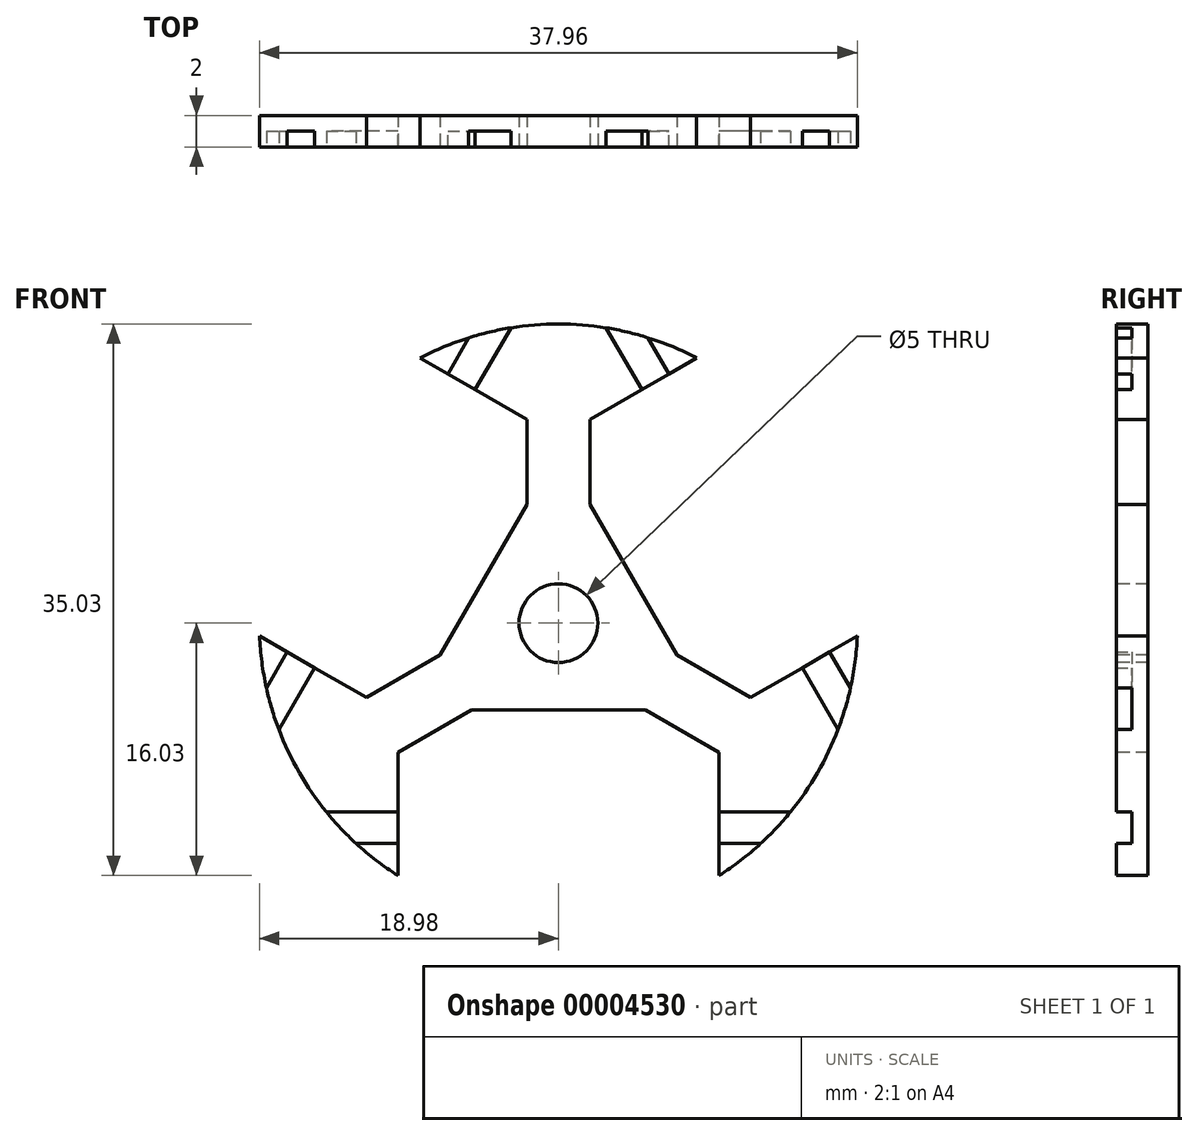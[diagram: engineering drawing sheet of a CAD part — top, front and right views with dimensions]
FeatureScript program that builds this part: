
annotation { "Feature Type Name" : "Feature", "Feature Type Description" : "" }
export const myFeature = defineFeature(function(context is Context, id is Id, definition is map)
    precondition{}
    {
        {
            var Q0;
            Q0=qCreatedBy(makeId("Front.planeOp"),FACE);
            var sketch = newSketch(context, id + "F0", { "sketchPlane" : qUnion([Q0])});
            skCircle(sketch, "E0", {"center": v(0, 0) * mm, "radius": 19 * mm, "construction": true});
            skCircle(sketch, "E1", {"center": v(0, 0) * mm, "radius": 20 * mm, "construction": true});
            skLineSegment(sketch, "E2", {"start": v(0, 0) * mm, "end": v(10, -17.32) * mm, "construction": true});
            skLineSegment(sketch, "E3", {"start": v(10, -17.32) * mm, "end": v(10, -8.08) * mm, "construction": true});
            skLineSegment(sketch, "E4", {"start": v(0, -13) * mm, "end": v(15.2, -13) * mm, "construction": true});
            skLineSegment(sketch, "E5", {"start": v(10, -12) * mm, "end": v(16, -12) * mm, "construction": true});
            skLineSegment(sketch, "E6", {"start": v(14.28, -14) * mm, "end": v(10, -14) * mm, "construction": true});
            skLineSegment(sketch, "E7", {"start": v(10.2, -8.2) * mm, "end": v(10.2, -16.03) * mm, "construction": true});
            skCircle(sketch, "E8", {"center": v(0, -26) * mm, "radius": 20 * mm, "construction": true});
            skLineSegment(sketch, "E9", {"start": v(0, -5.5) * mm, "end": v(5.53, -5.5) * mm, "construction": true});
            skLineSegment(sketch, "E10", {"start": v(0, 0) * mm, "end": v(17.32, -10) * mm, "construction": true});
            skLineSegment(sketch, "E11", {"start": v(10.2, -8.2) * mm, "end": v(5.53, -5.5) * mm, "construction": true});
            skLineSegment(sketch, "E12.0.MirrorCS", {"start": v(0, -5.5) * mm, "end": v(-5.53, -5.5) * mm, "construction": true});
            skLineSegment(sketch, "E12.1.MirrorCS", {"start": v(-14.28, -14) * mm, "end": v(-10, -14) * mm, "construction": true});
            skLineSegment(sketch, "E12.2.MirrorCS", {"start": v(-10, -12) * mm, "end": v(-16, -12) * mm, "construction": true});
            skLineSegment(sketch, "E12.3.MirrorCS", {"start": v(-10.2, -8.2) * mm, "end": v(-10.2, -16.03) * mm, "construction": true});
            skLineSegment(sketch, "E12.4.MirrorCS", {"start": v(0, -13) * mm, "end": v(-15.2, -13) * mm, "construction": true});
            skLineSegment(sketch, "E12.5.MirrorCS", {"start": v(-10, -17.32) * mm, "end": v(-10, -8.08) * mm, "construction": true});
            skLineSegment(sketch, "E12.6.MirrorCS", {"start": v(-10.2, -8.2) * mm, "end": v(-5.53, -5.5) * mm, "construction": true});
            skLineSegment(sketch, "E13.1.0", {"start": v(11.26, 6.5) * mm, "end": v(3.66, 19.66) * mm, "construction": true});
            skLineSegment(sketch, "E13.1.1", {"start": v(11.26, 6.5) * mm, "end": v(18.86, -6.66) * mm, "construction": true});
            skLineSegment(sketch, "E13.1.2", {"start": v(19.27, -5.37) * mm, "end": v(17.12, -1.66) * mm, "construction": true});
            skLineSegment(sketch, "E13.1.3", {"start": v(2, 12.93) * mm, "end": v(8.78, 16.85) * mm, "construction": true});
            skLineSegment(sketch, "E13.1.4", {"start": v(12.2, -4.73) * mm, "end": v(7.53, -2.04) * mm, "construction": true});
            skLineSegment(sketch, "E13.1.5", {"start": v(5.4, 14.66) * mm, "end": v(2.4, 19.86) * mm, "construction": true});
            skLineSegment(sketch, "E13.1.6", {"start": v(12.2, -4.73) * mm, "end": v(18.98, -0.82) * mm, "construction": true});
            skLineSegment(sketch, "E13.1.7", {"start": v(10, 17.32) * mm, "end": v(2, 12.7) * mm, "construction": true});
            skLineSegment(sketch, "E13.1.8", {"start": v(4.76, 2.75) * mm, "end": v(7.53, -2.04) * mm, "construction": true});
            skLineSegment(sketch, "E13.1.9", {"start": v(15.4, -2.66) * mm, "end": v(18.4, -7.86) * mm, "construction": true});
            skLineSegment(sketch, "E13.1.10", {"start": v(20, 0) * mm, "end": v(12, -4.62) * mm, "construction": true});
            skLineSegment(sketch, "E13.1.11", {"start": v(4.76, 2.75) * mm, "end": v(2, 7.54) * mm, "construction": true});
            skLineSegment(sketch, "E13.1.12", {"start": v(4.98, 19.37) * mm, "end": v(7.12, 15.66) * mm, "construction": true});
            skLineSegment(sketch, "E13.1.13", {"start": v(2, 12.93) * mm, "end": v(2, 7.54) * mm, "construction": true});
            skLineSegment(sketch, "E13.2.0", {"start": v(-11.26, 6.5) * mm, "end": v(-18.86, -6.66) * mm, "construction": true});
            skLineSegment(sketch, "E13.2.1", {"start": v(-11.26, 6.5) * mm, "end": v(-3.66, 19.66) * mm, "construction": true});
            skLineSegment(sketch, "E13.2.2", {"start": v(-4.98, 19.37) * mm, "end": v(-7.12, 15.66) * mm, "construction": true});
            skLineSegment(sketch, "E13.2.3", {"start": v(-12.2, -4.73) * mm, "end": v(-18.98, -0.82) * mm, "construction": true});
            skLineSegment(sketch, "E13.2.4", {"start": v(-2, 12.93) * mm, "end": v(-2, 7.54) * mm, "construction": true});
            skLineSegment(sketch, "E13.2.5", {"start": v(-15.4, -2.66) * mm, "end": v(-18.4, -7.86) * mm, "construction": true});
            skLineSegment(sketch, "E13.2.6", {"start": v(-2, 12.93) * mm, "end": v(-8.78, 16.85) * mm, "construction": true});
            skLineSegment(sketch, "E13.2.7", {"start": v(-20, 0) * mm, "end": v(-12, -4.62) * mm, "construction": true});
            skLineSegment(sketch, "E13.2.8", {"start": v(-4.76, 2.75) * mm, "end": v(-2, 7.54) * mm, "construction": true});
            skLineSegment(sketch, "E13.2.9", {"start": v(-5.4, 14.66) * mm, "end": v(-2.4, 19.86) * mm, "construction": true});
            skLineSegment(sketch, "E13.2.10", {"start": v(-10, 17.32) * mm, "end": v(-2, 12.7) * mm, "construction": true});
            skLineSegment(sketch, "E13.2.11", {"start": v(-4.76, 2.75) * mm, "end": v(-7.53, -2.04) * mm, "construction": true});
            skLineSegment(sketch, "E13.2.12", {"start": v(-19.27, -5.37) * mm, "end": v(-17.12, -1.66) * mm, "construction": true});
            skLineSegment(sketch, "E13.2.13", {"start": v(-12.2, -4.73) * mm, "end": v(-7.53, -2.04) * mm, "construction": true});
            skCircle(sketch, "E14", {"center": v(0, 0) * mm, "radius": 2.5 * mm, "construction": true});
            skSolve(sketch);
        }
        {
            var Q0;
            Q0=qCreatedBy(makeId("Front.planeOp"),FACE);
            var sketch = newSketch(context, id + "F1", { "sketchPlane" : qUnion([Q0])});
            skCircle(sketch, "E15.0", {"center": v(0, 0) * mm, "radius": 19 * mm});
            skSolve(sketch);
        }
        {
            var Q0;
            Q0=makeQuery(id+"F1.imprint","IMPRINT",FACE,{"disambiguationData":[TD([[makeQuery(id+"F1.imprint","IMPRINT",EDGE,{"derivedFrom":sQuery(id+"F1.wireOp",EDGE,"E15.0")}),1.0]])]});
            extrude(context, id + "F2", {"entities" : qUnion([Q0]), "oppositeDirection" : true, "depth" : 2 * mm});
        }
        {
            var Q0;
            Q0=qCreatedBy(makeId("Front.planeOp"),FACE);
            var sketch = newSketch(context, id + "F3", { "sketchPlane" : qUnion([Q0])});
            skLineSegment(sketch, "E16.0", {"start": v(-10.2, -8.2) * mm, "end": v(-10.2, -16.03) * mm});
            skLineSegment(sketch, "E16.1", {"start": v(-10.2, -8.2) * mm, "end": v(-5.53, -5.5) * mm});
            skLineSegment(sketch, "E16.2", {"start": v(0, -5.5) * mm, "end": v(-5.53, -5.5) * mm});
            skLineSegment(sketch, "E16.3", {"start": v(0, -5.5) * mm, "end": v(5.53, -5.5) * mm});
            skLineSegment(sketch, "E16.4", {"start": v(10.2, -8.2) * mm, "end": v(5.53, -5.5) * mm});
            skLineSegment(sketch, "E16.5", {"start": v(10.2, -8.2) * mm, "end": v(10.2, -16.03) * mm});
            skLineSegment(sketch, "E16.6", {"start": v(12.2, -4.73) * mm, "end": v(18.98, -0.82) * mm});
            skLineSegment(sketch, "E16.7", {"start": v(12.2, -4.73) * mm, "end": v(7.53, -2.04) * mm});
            skLineSegment(sketch, "E16.8", {"start": v(4.76, 2.75) * mm, "end": v(7.53, -2.04) * mm});
            skLineSegment(sketch, "E16.9", {"start": v(4.76, 2.75) * mm, "end": v(2, 7.54) * mm});
            skLineSegment(sketch, "E16.10", {"start": v(2, 12.93) * mm, "end": v(2, 7.54) * mm});
            skLineSegment(sketch, "E16.11", {"start": v(2, 12.93) * mm, "end": v(8.78, 16.85) * mm});
            skLineSegment(sketch, "E16.12", {"start": v(-2, 12.93) * mm, "end": v(-8.78, 16.85) * mm});
            skLineSegment(sketch, "E16.13", {"start": v(-2, 12.93) * mm, "end": v(-2, 7.54) * mm});
            skLineSegment(sketch, "E16.14", {"start": v(-4.76, 2.75) * mm, "end": v(-2, 7.54) * mm});
            skLineSegment(sketch, "E16.15", {"start": v(-4.76, 2.75) * mm, "end": v(-7.53, -2.04) * mm});
            skLineSegment(sketch, "E16.16", {"start": v(-12.2, -4.73) * mm, "end": v(-7.53, -2.04) * mm});
            skLineSegment(sketch, "E16.17", {"start": v(-12.2, -4.73) * mm, "end": v(-18.98, -0.82) * mm});
            skArc(sketch, "E17", {"start": v(-8.78, 16.85) * mm, "mid": v(-16.45, 9.5) * mm, "end": v(-18.98, -0.82) * mm});
            skArc(sketch, "E18", {"start": v(18.98, -0.82) * mm, "mid": v(16.45, 9.5) * mm, "end": v(8.78, 16.85) * mm});
            skArc(sketch, "E19", {"start": v(-10.2, -16.03) * mm, "mid": v(0, -19) * mm, "end": v(10.2, -16.03) * mm});
            skCircle(sketch, "E20.0", {"center": v(0, 0) * mm, "radius": 2.5 * mm});
            skSolve(sketch);
        }
        {
            var Q0;
            Q0=makeQuery(id+"F3.imprint","IMPRINT",FACE,{"disambiguationData":[TD([[makeQuery(id+"F3.imprint","IMPRINT",EDGE,{"derivedFrom":sQuery(id+"F3.wireOp",EDGE,"E16.12")}),1.0]])]});
            var Q1;
            Q1=makeQuery(id+"F3.imprint","IMPRINT",FACE,{"disambiguationData":[TD([[makeQuery(id+"F3.imprint","IMPRINT",EDGE,{"derivedFrom":sQuery(id+"F3.wireOp",EDGE,"E16.6")}),1.0]])]});
            var Q2;
            Q2=makeQuery(id+"F3.imprint","IMPRINT",FACE,{"disambiguationData":[TD([[makeQuery(id+"F3.imprint","IMPRINT",EDGE,{"derivedFrom":sQuery(id+"F3.wireOp",EDGE,"E16.0")}),1.0]])]});
            var Q3;
            Q3=makeQuery(id+"F3.imprint","IMPRINT",FACE,{"disambiguationData":[TD([[makeQuery(id+"F3.imprint","IMPRINT",EDGE,{"derivedFrom":sQuery(id+"F3.wireOp",EDGE,"E20.0")}),1.0]])]});
            extrude(context, id + "F4", {"entities" : qUnion([Q0, Q1, Q2, Q3]), "operationType" : NewBodyOperationType.REMOVE, "endBound" : BoundingType.UP_TO_NEXT, "oppositeDirection" : true, "depth" : 25 * mm});
        }
        {
            var Q0;
            Q0=qCreatedBy(makeId("Right.planeOp"),FACE);
            var sketch = newSketch(context, id + "F5", { "sketchPlane" : qUnion([Q0])});
            skLineSegment(sketch, "E21.rect.bottom", {"start": v(-1, -14) * mm, "end": v(1, -14) * mm});
            skLineSegment(sketch, "E21.rect.top", {"start": v(-1, -12) * mm, "end": v(1, -12) * mm});
            skLineSegment(sketch, "E21.rect.left", {"start": v(-1, -14) * mm, "end": v(-1, -12) * mm});
            skLineSegment(sketch, "E21.rect.right", {"start": v(1, -14) * mm, "end": v(1, -12) * mm});
            skPoint(sketch, "E21.rect.middle", {"position": v(0, -13) * mm});
            skSolve(sketch);
        }
        {
            var Q0;
            Q0=makeQuery(id+"F5.imprint","IMPRINT",FACE,{"disambiguationData":[TD([[makeQuery(id+"F5.imprint","IMPRINT",EDGE,{"derivedFrom":sQuery(id+"F5.wireOp",EDGE,"E21.rect.bottom")}),1.0]])]});
            extrude(context, id + "F6", {"entities" : qUnion([Q0]), "endBound" : BoundingType.SYMMETRIC, "depth" : 40 * mm});
        }
        {
            var Q0;
            Q0=qCreatedBy(makeId("Top.planeOp"),FACE);
            var sketch = newSketch(context, id + "F7", { "sketchPlane" : qUnion([Q0])});
            skLineSegment(sketch, "E22", {"start": v(0, 0) * mm, "end": v(0, 2) * mm, "construction": true});
            skSolve(sketch);
        }
        {
            var Q0;
            Q0=makeQuery(id+"F6.opExtrude","SWEPT_BODY",BODY,{"disambiguationData":[OSD([sQuery(id+"F5.wireOp",EDGE,"E21.rect.bottom"),sQuery(id+"F5.wireOp",EDGE,"E21.rect.top"),sQuery(id+"F5.wireOp",EDGE,"E21.rect.left"),sQuery(id+"F5.wireOp",EDGE,"E21.rect.right")])]});
            var Q1;
            Q1=sQuery(id+"F7.wireOp",EDGE,"E22");
            circularPattern(context, id + "F8", {"entities" : qUnion([Q0]), "axis" : qUnion([Q1]), "angle" : 120 * degree, "instanceCount" : round(3)});
        }
        {
            var Q0;
            Q0=makeQuery(id+"F8.opPattern","COPY",BODY,{"derivedFrom":makeQuery(id+"F6.opExtrude","SWEPT_BODY",BODY,{"disambiguationData":[OSD([sQuery(id+"F5.wireOp",EDGE,"E21.rect.bottom"),sQuery(id+"F5.wireOp",EDGE,"E21.rect.top"),sQuery(id+"F5.wireOp",EDGE,"E21.rect.left"),sQuery(id+"F5.wireOp",EDGE,"E21.rect.right")])]}),"instanceName":"1"});
            var Q1;
            Q1=makeQuery(id+"F8.opPattern","COPY",BODY,{"derivedFrom":makeQuery(id+"F6.opExtrude","SWEPT_BODY",BODY,{"disambiguationData":[OSD([sQuery(id+"F5.wireOp",EDGE,"E21.rect.bottom"),sQuery(id+"F5.wireOp",EDGE,"E21.rect.top"),sQuery(id+"F5.wireOp",EDGE,"E21.rect.left"),sQuery(id+"F5.wireOp",EDGE,"E21.rect.right")])]}),"instanceName":"2"});
            var Q2;
            Q2=makeQuery(id+"F6.opExtrude","SWEPT_BODY",BODY,{"disambiguationData":[OSD([sQuery(id+"F5.wireOp",EDGE,"E21.rect.bottom"),sQuery(id+"F5.wireOp",EDGE,"E21.rect.top"),sQuery(id+"F5.wireOp",EDGE,"E21.rect.left"),sQuery(id+"F5.wireOp",EDGE,"E21.rect.right")])]});
            var Q3;
            Q3=makeQuery(id+"F2.opExtrude","SWEPT_BODY",BODY,{"disambiguationData":[OSD([sQuery(id+"F1.wireOp",EDGE,"E15.0")])]});
            booleanBodies(context, id + "F9", {"operationType" : BooleanOperationType.SUBTRACTION, "tools" : qUnion([Q0, Q1, Q2]), "targets" : qUnion([Q3])});
        }
    });
